# Revit family: 56_WTH_RUH-N verdeler_e
name_source: partatom
category: Mechanical Equipment
revit_build: Autodesk Revit MEP 2012 (Build: 20110916_2132(x64)
units: mm (PartAtom-declared; Revit-internal decimal feet)

## types (13) — shared parameters
Content version = 1.0
Description = Regelunit met pomp geschikt voor naregeling
Manufacturer = WTH Vloerverwarming B.V.
URL = http://www.wth.nl
content_modified_date = 08-08-2013
datasheet = http://www.wth.nl
hoh = 60 mm  [stored 0.19685 ft]
len3 = 40.3 mm  [stored 0.132218 ft]
leverancier = WTH Vloerverwarming B.V.
lod_niveau = LOD400
type pomp = CGA_u buisconstructie RUHN_f : 00_CGA_u-buisconstructie RUH-N_f

## per-type parameters (varying)
| type | aant | aantal groepen | artikelnummer | bestelnummer | lengte verdeler | lengte verzamelaar |
| RUH-N2 | 2 | 2 | G142 | G142 | 272.9 mm  [stored 0.895341 ft] | 171.8 mm  [stored 0.563648 ft] |
| RUH-N3 | 3 | 3 | G143 | G143 | 332.9 mm  [stored 1.09219 ft] | 231.8 mm |
| RUH-N4 | 4 | 4 | G144 | G144 | 392.9 mm | 291.8 mm |
| RUH-N5 | 5 | 5 | G145 | G145 | 452.9 mm  [stored 1.48589 ft] | 351.8 mm  [stored 1.1542 ft] |
| RUH-N6 | 6 | 6 | G146 | G146 | 512.9 mm | 411.8 mm  [stored 1.35105 ft] |
| RUH-N7 | 7 | 7 | G147 | G147 | 572.9 mm  [stored 1.87959 ft] | 471.8 mm |
| RUH-N8 | 8 | 8 | G148 | G148 | 632.9 mm  [stored 2.07644 ft] | 531.8 mm  [stored 1.74475 ft] |
| RUH-N9 | 9 | 9 | G149 | G149 | 692.9 mm  [stored 2.27329 ft] | 591.8 mm |
| RUH-N10 | 10 | 10 | G150 | G150 | 752.9 mm  [stored 2.47014 ft] | 651.8 mm  [stored 2.13845 ft] |
| RUH-N11 | 11 | 11 | G151 | G151 | 812.9 mm  [stored 2.66699 ft] | 711.8 mm  [stored 2.3353 ft] |
| RUH-N12 | 12 | 12 | G152 | G152 | 872.9 mm  [stored 2.86385 ft] | 771.8 mm  [stored 2.53215 ft] |
| RUH-N14 | 14 | 14 | G154 | G154 | 992.9 mm  [stored 3.25755 ft] | 891.8 mm  [stored 2.92585 ft] |
| RUH-N16 | 16 | 16 | G156 | G156 | 1112.9 mm | 1011.8 mm  [stored 3.31955 ft] |

note: column(s) folded — value = type name in every type: Model

note: [stored X ft] marks values corroborated as IEEE doubles in the binary element streams (Revit-internal decimal feet)

## geometry (parser evidence)
native form markers: Blend x4, Sweep x38
no freeform markers — native parametric forms only
